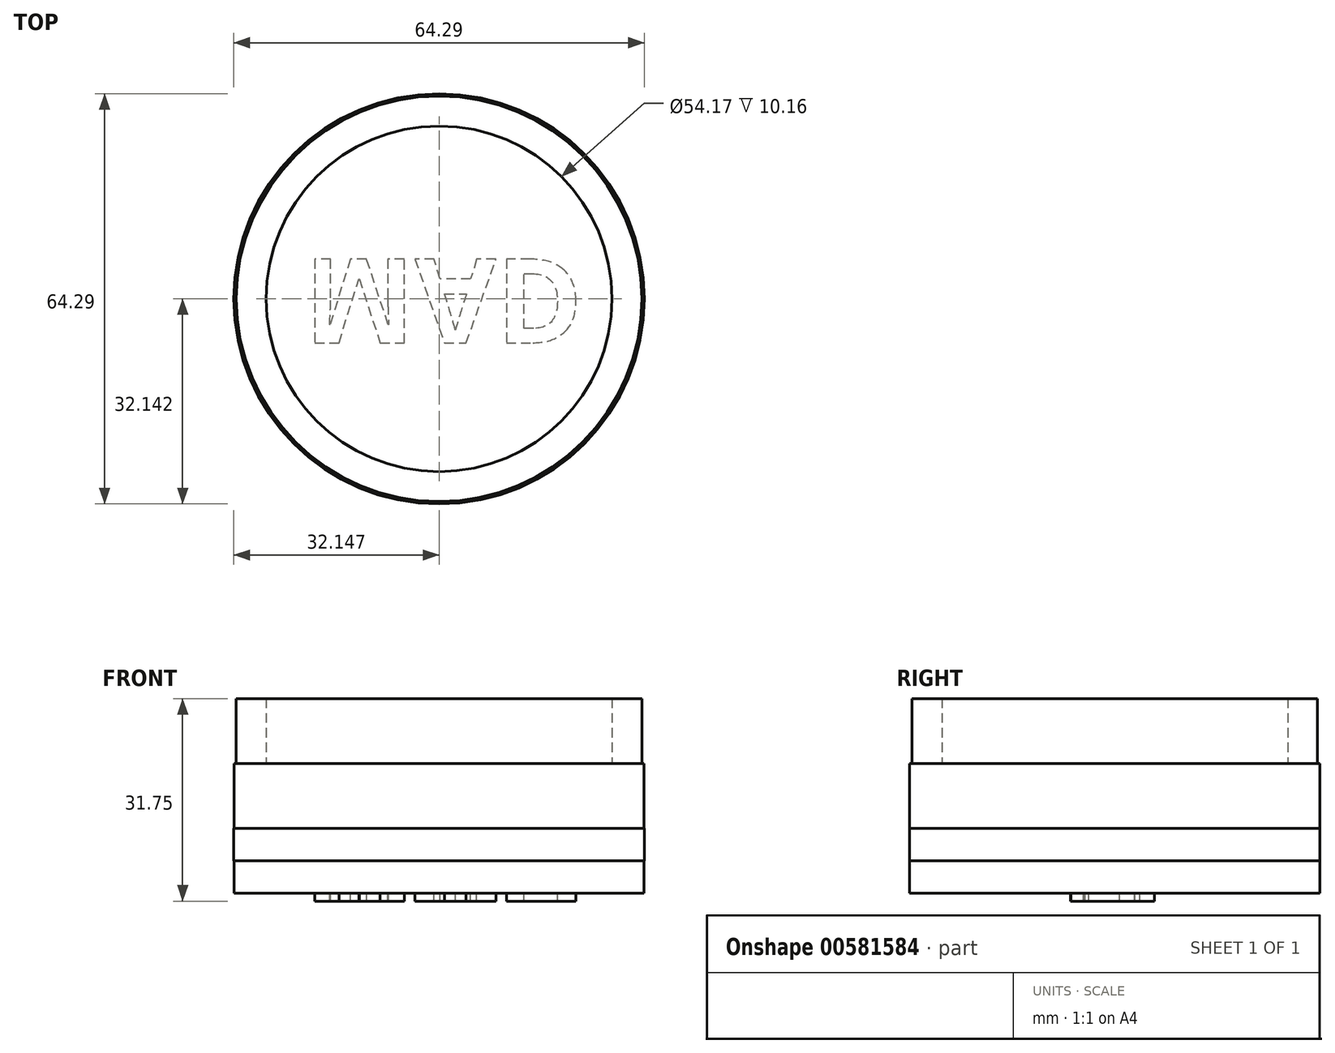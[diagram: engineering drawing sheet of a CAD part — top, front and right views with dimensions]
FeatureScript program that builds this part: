
annotation { "Feature Type Name" : "Feature", "Feature Type Description" : "" }
export const myFeature = defineFeature(function(context is Context, id is Id, definition is map)
    precondition{}
    {
        {
            var Q0;
            Q0=qCreatedBy(makeId("Top.planeOp"),FACE);
            var sketch = newSketch(context, id + "F0", { "sketchPlane" : qUnion([Q0])});
            skCircle(sketch, "E0", {"center": v(-41.42, 38.27) * mm, "radius": 32.12 * mm});
            skSolve(sketch);
        }
        {
            var Q0;
            Q0 = qSketchRegion(id + "F0", true);
            extrude(context, id + "F1", {"entities" : qUnion([Q0]), "depth" : 5.08 * mm, "offsetDistance" : 25.4 * mm});
        }
        {
            var Q0;
            Q0=makeQuery(id+"F1.opExtrude","CAP_FACE",FACE,{"disambiguationData":[OSD([sQuery(id+"F0.wireOp",EDGE,"E0")])],"isStart":false});
            var sketch = newSketch(context, id + "F2", { "sketchPlane" : qUnion([Q0])});
            skCircle(sketch, "E1", {"center": v(-41.42, 38.27) * mm, "radius": 32.14 * mm});
            skSolve(sketch);
        }
        {
            var Q0;
            Q0 = qSketchRegion(id + "F2", true);
            extrude(context, id + "F3", {"entities" : qUnion([Q0]), "operationType" : NewBodyOperationType.ADD, "depth" : 5.08 * mm, "offsetDistance" : 25.4 * mm});
        }
        {
            var Q0;
            Q0=makeQuery(id+"F3.opExtrude","CAP_FACE",FACE,{"disambiguationData":[OSD([sQuery(id+"F2.wireOp",EDGE,"E1")])],"isStart":false});
            var sketch = newSketch(context, id + "F4", { "sketchPlane" : qUnion([Q0])});
            skCircle(sketch, "E2", {"center": v(-41.42, 38.27) * mm, "radius": 31.77 * mm});
            skCircle(sketch, "E3", {"center": v(-41.42, 38.27) * mm, "radius": 27.09 * mm});
            skSolve(sketch);
        }
        {
            var Q0;
            Q0 = qSketchRegion(id + "F4", true);
            var Q1;
            Q1=makeQuery(id+"F1.opExtrude","CAP_FACE",FACE,{"disambiguationData":[OSD([sQuery(id+"F0.wireOp",EDGE,"E0")])],"isStart":true});
            extrude(context, id + "F5", {"entities" : qUnion([Q0, Q1]), "operationType" : NewBodyOperationType.ADD, "depth" : 20.32 * mm, "offsetDistance" : 25.4 * mm});
        }
        {
            var Q0;
            Q0=makeQuery(id+"F1.opExtrude","CAP_FACE",FACE,{"disambiguationData":[OSD([sQuery(id+"F0.wireOp",EDGE,"E0")])],"isStart":true});
            var sketch = newSketch(context, id + "F6", { "sketchPlane" : qUnion([Q0])});
            skText(sketch, "E4", { "text": "MAD", "fontName": "NotoSans-Bold.ttf"});
            const initialGuessF6  = {"E4": [-0.06253, -0.0445, 1, 0, 0.01323]};
            skSetInitialGuess(sketch, initialGuessF6);
            skSolve(sketch);
        }
        {
            var Q0;
            Q0 = qSketchRegion(id + "F6", true);
            extrude(context, id + "F7", {"entities" : qUnion([Q0]), "operationType" : NewBodyOperationType.ADD, "depth" : 1.27 * mm, "offsetDistance" : 25.4 * mm});
        }
    });
